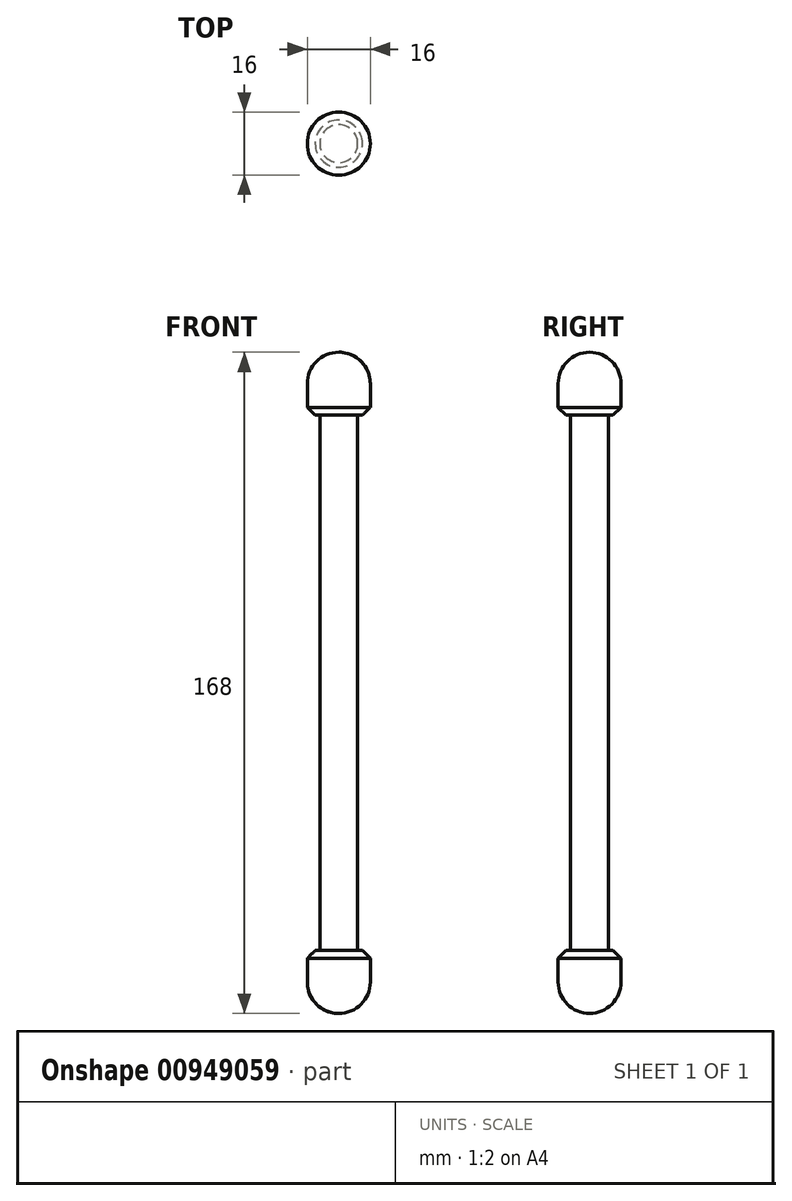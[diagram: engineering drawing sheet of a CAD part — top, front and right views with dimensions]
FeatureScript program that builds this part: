
annotation { "Feature Type Name" : "Feature", "Feature Type Description" : "" }
export const myFeature = defineFeature(function(context is Context, id is Id, definition is map)
    precondition{}
    {
        {
            var Q0;
            Q0=qCreatedBy(makeId("Top.planeOp"),FACE);
            var sketch = newSketch(context, id + "F0", { "sketchPlane" : qUnion([Q0])});
            skCircle(sketch, "E0", {"center": v(0, 0) * mm, "radius": 4.8 * mm});
            skSolve(sketch);
        }
        {
            var Q0;
            Q0 = qSketchRegion(id + "F0", true);
            extrude(context, id + "F1", {"entities" : qUnion([Q0]), "depth" : 136 * mm, "offsetDistance" : 25 * mm});
        }
        {
            var Q0;
            Q0=makeQuery(id+"F1.opExtrude","CAP_FACE",FACE,{"disambiguationData":[OSD([sQuery(id+"F0.wireOp",EDGE,"E0")])],"isStart":true});
            var sketch = newSketch(context, id + "F2", { "sketchPlane" : qUnion([Q0])});
            skCircle(sketch, "E1", {"center": v(0, 0) * mm, "radius": 8 * mm});
            skSolve(sketch);
        }
        {
            var Q0;
            Q0 = qSketchRegion(id + "F2", true);
            extrude(context, id + "F3", {"entities" : qUnion([Q0]), "operationType" : NewBodyOperationType.ADD, "depth" : 16 * mm, "offsetDistance" : 25 * mm});
        }
        {
            var Q0;
            Q0=makeQuery(id+"F1.opExtrude","CAP_FACE",FACE,{"disambiguationData":[OSD([sQuery(id+"F0.wireOp",EDGE,"E0")])],"isStart":false});
            var sketch = newSketch(context, id + "F4", { "sketchPlane" : qUnion([Q0])});
            skCircle(sketch, "E2.0.0", {"center": v(0, 0) * mm, "radius": 8 * mm});
            skSolve(sketch);
        }
        {
            var Q0;
            Q0 = qSketchRegion(id + "F4", true);
            extrude(context, id + "F5", {"entities" : qUnion([Q0]), "operationType" : NewBodyOperationType.ADD, "depth" : 16 * mm, "offsetDistance" : 25 * mm});
        }
        {
            var Q0;
            Q0=makeQuery(id+"F3.opExtrude","CAP_EDGE",EDGE,{"disambiguationData":[OSD([sQuery(id+"F2.wireOp",EDGE,"E1")])],"isStart":false});
            var Q1;
            Q1=makeQuery(id+"F5.opExtrude","CAP_EDGE",EDGE,{"disambiguationData":[OSD([sQuery(id+"F4.wireOp",EDGE,"E2.0.0")])],"isStart":false});
            fillet(context, id + "F6", {"entities" : qUnion([Q0, Q1]), "radius" : 8 * mm, "tangentPropagation" : true, "allowEdgeOverflow" : false});
        }
        {
            var Q0;
            Q0=makeQuery(id+"F3.opExtrude","CAP_EDGE",EDGE,{"disambiguationData":[OSD([sQuery(id+"F2.wireOp",EDGE,"E1")])],"isStart":true});
            var Q1;
            Q1=makeQuery(id+"F5.opExtrude","CAP_EDGE",EDGE,{"disambiguationData":[OSD([sQuery(id+"F4.wireOp",EDGE,"E2.0.0")])],"isStart":true});
            chamfer(context, id + "F7", {"entities" : qUnion([Q0, Q1]), "width" : 2 * mm, "tangentPropagation" : true});
        }
    });
